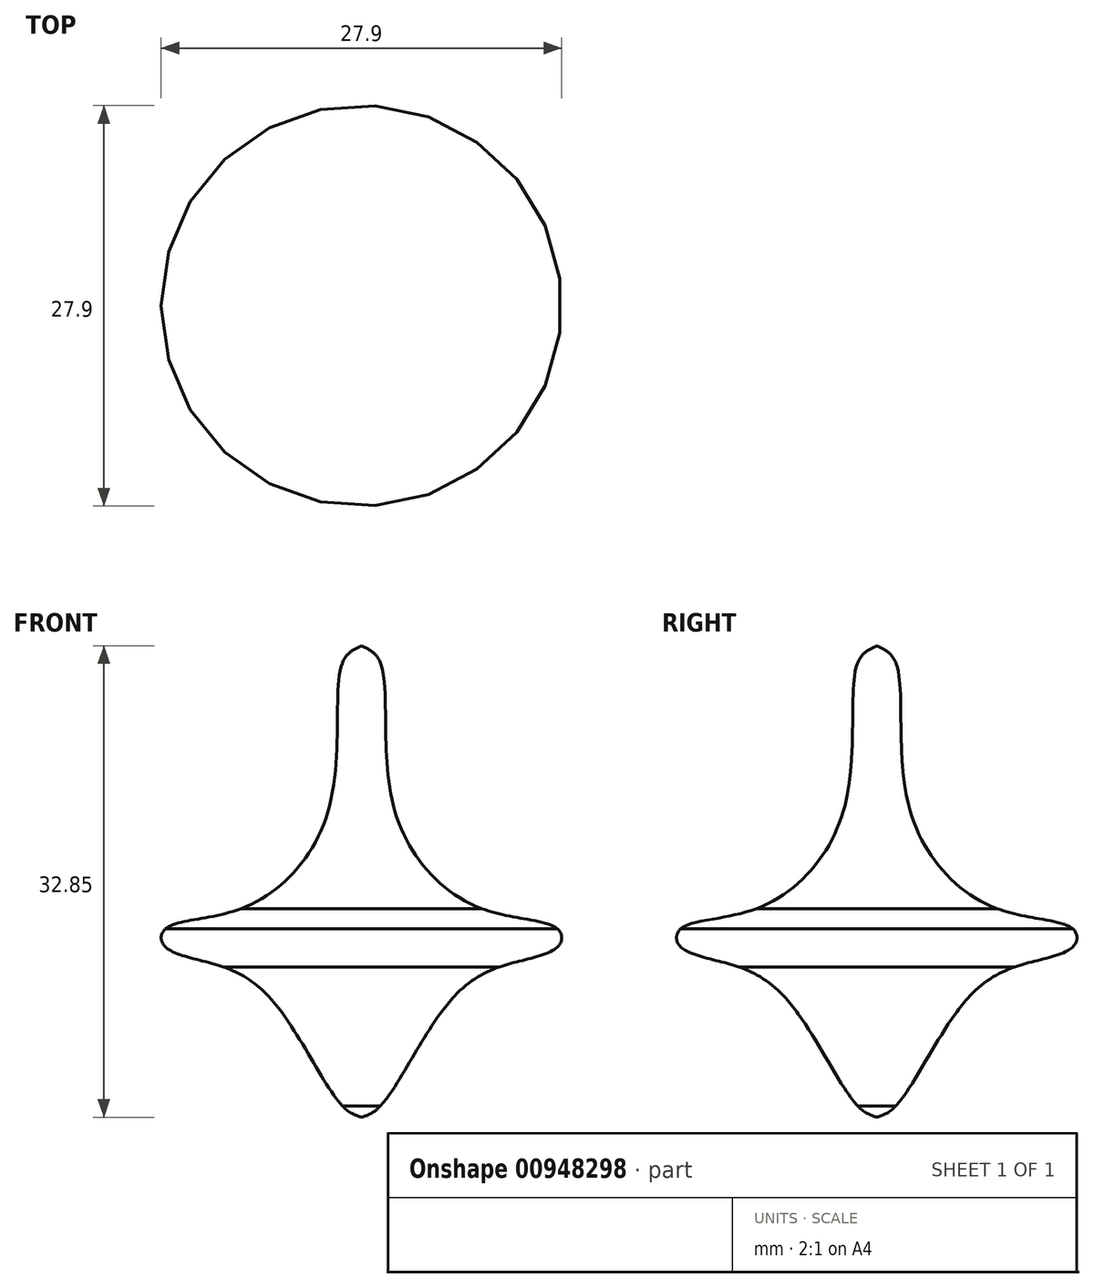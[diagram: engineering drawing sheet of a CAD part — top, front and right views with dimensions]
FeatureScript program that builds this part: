
annotation { "Feature Type Name" : "Feature", "Feature Type Description" : "" }
export const myFeature = defineFeature(function(context is Context, id is Id, definition is map)
    precondition{}
    {
        {
            var Q0;
            Q0=qCreatedBy(makeId("Front.planeOp"),FACE);
            var sketch = newSketch(context, id + "F0", { "sketchPlane" : qUnion([Q0])});
            skLineSegment(sketch, "E0", {"start": v(0, 0) * mm, "end": v(0, 19.73) * mm});
            skLineSegment(sketch, "E1", {"start": v(0, 0) * mm, "end": v(0, -13.12) * mm});
            skLineSegment(sketch, "E2", {"start": v(0, 18.5) * mm, "end": v(1.34, 18.5) * mm});
            skLineSegment(sketch, "E3", {"start": v(0, 8.6) * mm, "end": v(2.22, 8.6) * mm});
            skLineSegment(sketch, "E4", {"start": v(0, 1.42) * mm, "end": v(8.38, 1.42) * mm});
            skLineSegment(sketch, "E5", {"start": v(0, 0) * mm, "end": v(13.67, 0) * mm});
            skLineSegment(sketch, "E6", {"start": v(0, -1.2) * mm, "end": v(13.71, -1.2) * mm});
            skLineSegment(sketch, "E7", {"start": v(0, -2.65) * mm, "end": v(9.6, -2.65) * mm});
            skLineSegment(sketch, "E8", {"start": v(0, -5.92) * mm, "end": v(5.47, -5.92) * mm});
            skLineSegment(sketch, "E9", {"start": v(0, -12.34) * mm, "end": v(1.32, -12.34) * mm});
            skFitSpline(sketch, "E10", {"points": [v(0, 19.73) * mm, v(1.34, 18.5) * mm, v(2.22, 8.6) * mm, v(8.38, 1.42) * mm, v(13.67, 0) * mm, v(13.71, -1.2) * mm, v(9.6, -2.65) * mm, v(5.47, -5.92) * mm, v(1.32, -12.34) * mm, v(0, -13.12) * mm], "startDerivative": vector(22.91, -10.32) * mm, "endDerivative": vector(-19.32, -5.95) * mm});
            skSolve(sketch);
        }
        {
            var Q0;
            Q0 = qSketchRegion(id + "F0", true);
            var Q1;
            Q1=sQuery(id+"F0.wireOp",EDGE,"E0");
            revolve(context, id + "F1", {"surfaceOperationType" : NewSurfaceOperationType.NEW, "entities" : qUnion([Q0]), "axis" : qUnion([Q1]), "revolveType" : RevolveType.FULL});
        }
    });
